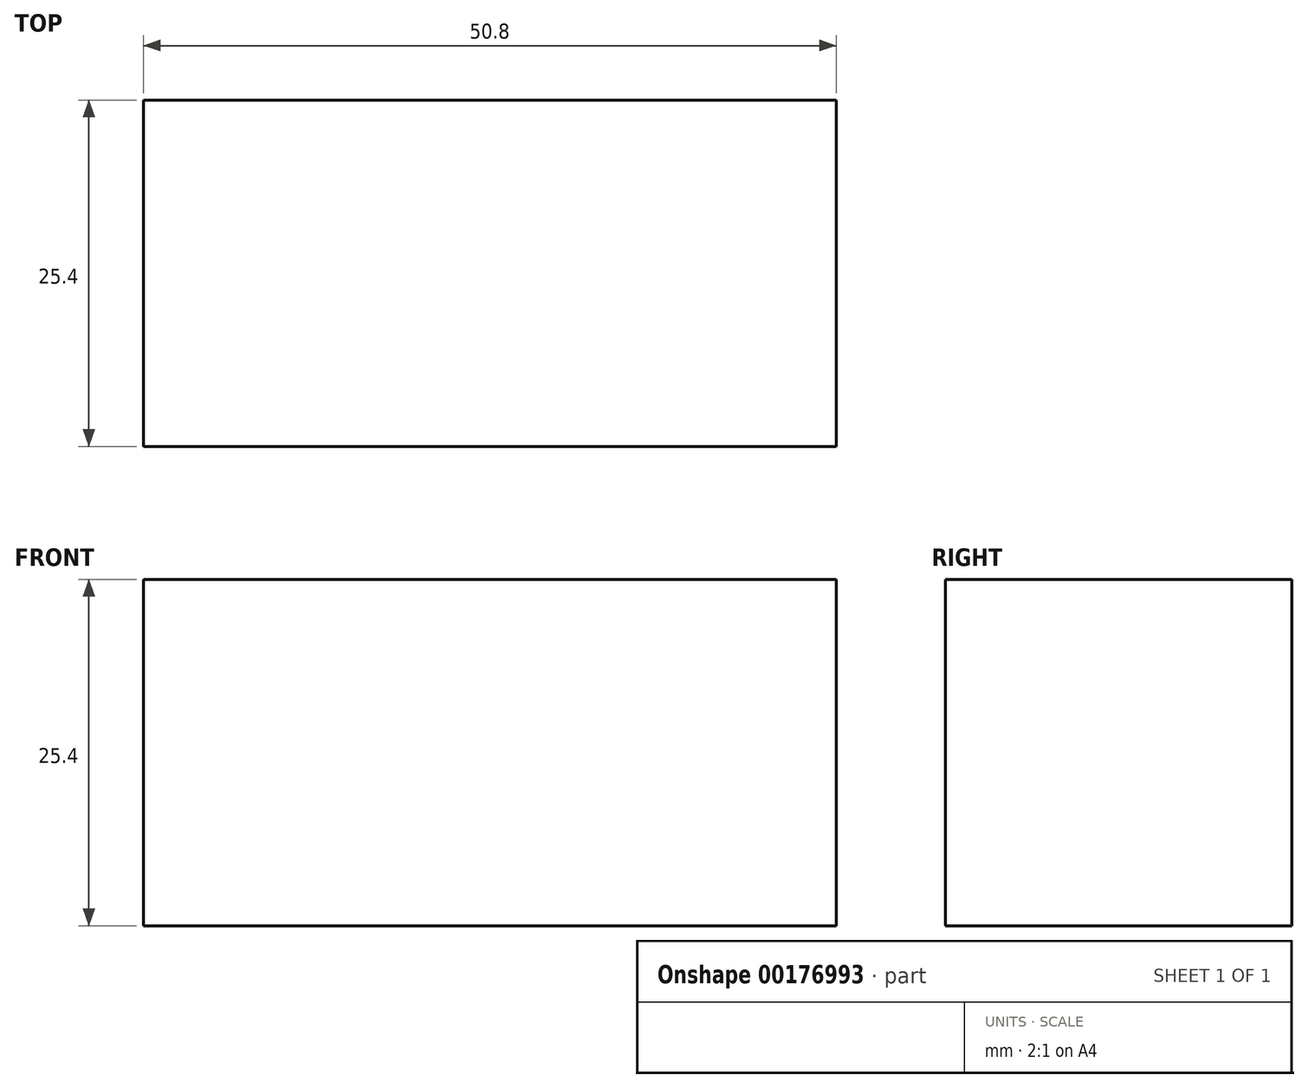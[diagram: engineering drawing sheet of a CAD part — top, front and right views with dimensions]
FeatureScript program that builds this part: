
annotation { "Feature Type Name" : "Feature", "Feature Type Description" : "" }
export const myFeature = defineFeature(function(context is Context, id is Id, definition is map)
    precondition{}
    {
        {
            var Q0;
            Q0=qCreatedBy(makeId("Top.planeOp"),FACE);
            var sketch = newSketch(context, id + "F0", { "sketchPlane" : qUnion([Q0])});
            skLineSegment(sketch, "E0.bottom", {"start": v(-74.25, -47.72) * mm, "end": v(-23.45, -47.72) * mm});
            skLineSegment(sketch, "E0.top", {"start": v(-74.25, -22.32) * mm, "end": v(-23.45, -22.32) * mm});
            skLineSegment(sketch, "E0.left", {"start": v(-74.25, -47.72) * mm, "end": v(-74.25, -22.32) * mm});
            skLineSegment(sketch, "E0.right", {"start": v(-23.45, -47.72) * mm, "end": v(-23.45, -22.32) * mm});
            skSolve(sketch);
        }
        {
            var Q0;
            Q0 = qSketchRegion(id + "F0", true);
            extrude(context, id + "F1", {"entities" : qUnion([Q0]), "depth" : 25.4 * mm});
        }
    });
